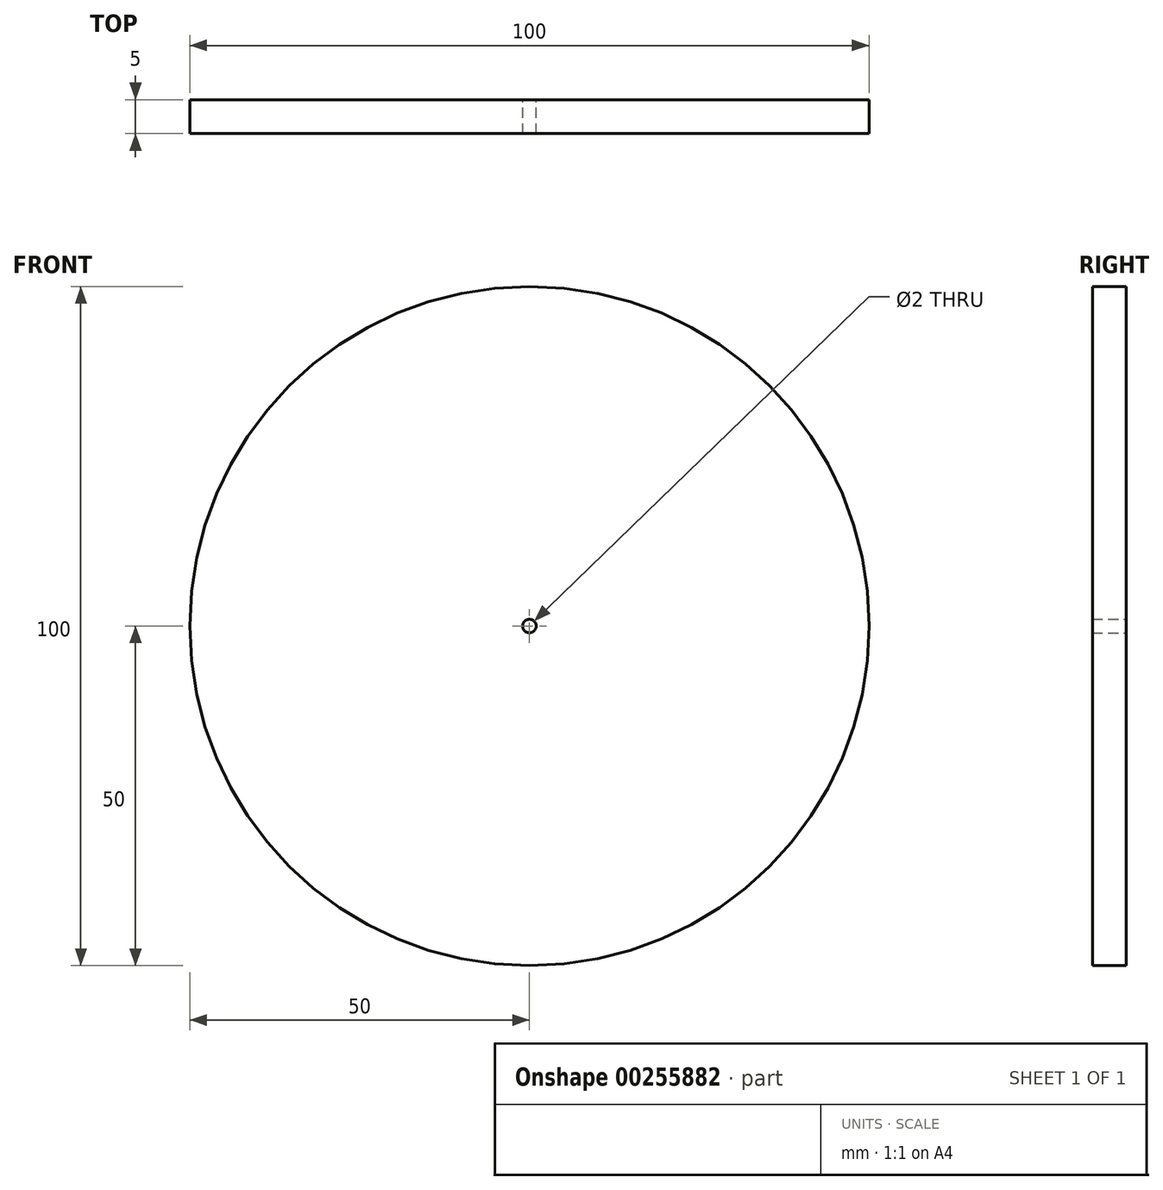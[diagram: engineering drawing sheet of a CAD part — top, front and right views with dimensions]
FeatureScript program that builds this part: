
annotation { "Feature Type Name" : "Feature", "Feature Type Description" : "" }
export const myFeature = defineFeature(function(context is Context, id is Id, definition is map)
    precondition{}
    {
        {
            var Q0;
            Q0=qCreatedBy(makeId("Front.planeOp"),FACE);
            var sketch = newSketch(context, id + "F0", { "sketchPlane" : qUnion([Q0])});
            skCircle(sketch, "E0", {"center": v(0, 0) * mm, "radius": 50 * mm});
            skSolve(sketch);
        }
        {
            var Q0;
            Q0=makeQuery(id+"F0.imprint","IMPRINT",FACE,{"disambiguationData":[TD([[makeQuery(id+"F0.imprint","IMPRINT",EDGE,{"derivedFrom":sQuery(id+"F0.wireOp",EDGE,"E0")}),1.0]])]});
            extrude(context, id + "F1", {"entities" : qUnion([Q0]), "depth" : 5 * mm});
        }
        {
            var Q0;
            Q0=sQuery(id+"F0.wireOp",VERTEX,"E0.center");
            var Q1;
            Q1=makeQuery(id+"F1.opExtrude","SWEPT_BODY",BODY,{"disambiguationData":[OSD([sQuery(id+"F0.wireOp",EDGE,"E0")])]});
            hole(context, id + "F2", {"style" : HoleStyle.SIMPLE, "endStyle" : HoleEndStyle.THROUGH, "oppositeDirection" : true, "holeDiameter" : 2 * mm, "isTappedThrough" : true, "tappedDepth" : 12 * mm, "tapClearance" : 3, "startFromSketch" : true, "locations" : qUnion([Q0]), "scope" : qUnion([Q1])});
        }
    });
